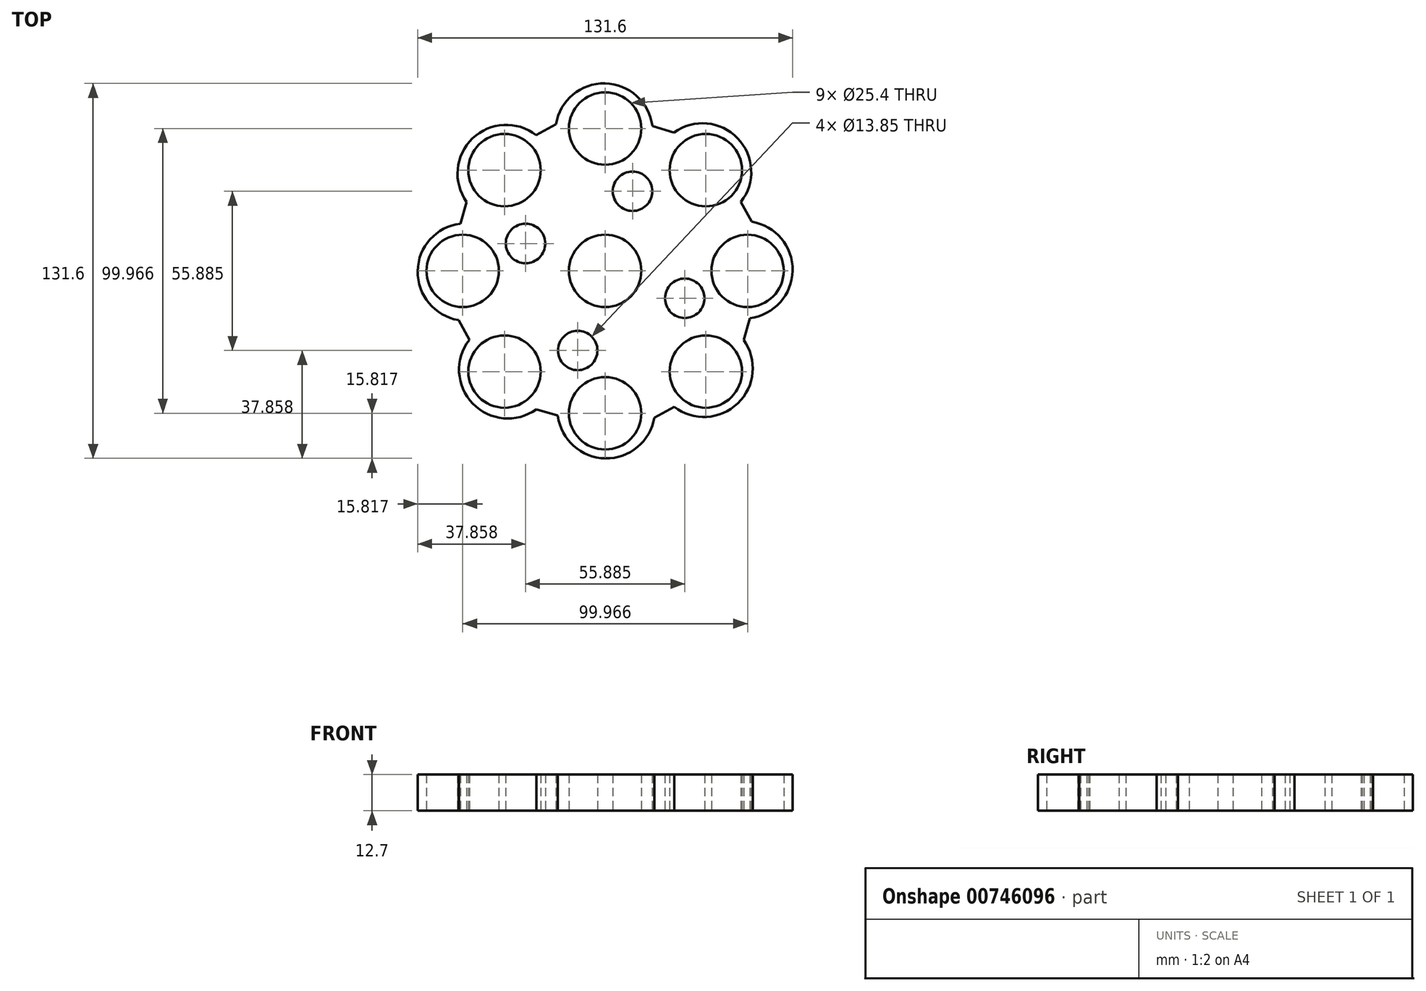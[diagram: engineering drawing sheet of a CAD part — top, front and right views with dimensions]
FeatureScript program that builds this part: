
annotation { "Feature Type Name" : "Feature", "Feature Type Description" : "" }
export const myFeature = defineFeature(function(context is Context, id is Id, definition is map)
    precondition{}
    {
        {
            var Q0;
            Q0=qCreatedBy(makeId("Top.planeOp"),FACE);
            var sketch = newSketch(context, id + "F0", { "sketchPlane" : qUnion([Q0])});
            skCircle(sketch, "E0", {"center": v(0, 0) * mm, "radius": 12.7 * mm});
            skCircle(sketch, "E1", {"center": v(0, 49.98) * mm, "radius": 12.7 * mm});
            skCircle(sketch, "E2.1.0", {"center": v(-35.34, 35.34) * mm, "radius": 12.7 * mm});
            skCircle(sketch, "E2.2.0", {"center": v(-49.98, 0) * mm, "radius": 12.7 * mm});
            skCircle(sketch, "E2.3.0", {"center": v(-35.34, -35.34) * mm, "radius": 12.7 * mm});
            skCircle(sketch, "E2.4.0", {"center": v(0, -49.98) * mm, "radius": 12.7 * mm});
            skCircle(sketch, "E2.5.0", {"center": v(35.34, -35.34) * mm, "radius": 12.7 * mm});
            skCircle(sketch, "E2.6.0", {"center": v(49.98, 0) * mm, "radius": 12.7 * mm});
            skCircle(sketch, "E2.7.0", {"center": v(35.34, 35.34) * mm, "radius": 12.7 * mm});
            skArc(sketch, "E3", {"start": v(16.58, 50.83) * mm, "mid": v(-0.06, 65.8) * mm, "end": v(-17.26, 51.47) * mm});
            skArc(sketch, "E4.1.0", {"start": v(-24.21, 47.66) * mm, "mid": v(-46.57, 46.49) * mm, "end": v(-48.6, 24.2) * mm});
            skArc(sketch, "E4.2.0", {"start": v(-50.83, 16.58) * mm, "mid": v(-65.8, -0.06) * mm, "end": v(-51.47, -17.26) * mm});
            skArc(sketch, "E4.3.0", {"start": v(-47.66, -24.21) * mm, "mid": v(-46.49, -46.57) * mm, "end": v(-24.2, -48.6) * mm});
            skArc(sketch, "E4.4.0", {"start": v(-16.58, -50.83) * mm, "mid": v(0.06, -65.8) * mm, "end": v(17.26, -51.47) * mm});
            skArc(sketch, "E4.5.0", {"start": v(24.21, -47.66) * mm, "mid": v(46.57, -46.49) * mm, "end": v(48.6, -24.2) * mm});
            skArc(sketch, "E4.6.0", {"start": v(50.83, -16.58) * mm, "mid": v(65.8, 0.06) * mm, "end": v(51.47, 17.26) * mm});
            skArc(sketch, "E4.7.0", {"start": v(47.66, 24.21) * mm, "mid": v(46.49, 46.57) * mm, "end": v(24.2, 48.6) * mm});
            skLineSegment(sketch, "E5", {"start": v(-24.21, 47.66) * mm, "end": v(-17.26, 51.47) * mm});
            skLineSegment(sketch, "E6.1.0", {"start": v(-50.83, 16.58) * mm, "end": v(-48.6, 24.2) * mm});
            skLineSegment(sketch, "E6.2.0", {"start": v(-47.66, -24.21) * mm, "end": v(-51.47, -17.26) * mm});
            skLineSegment(sketch, "E6.3.0", {"start": v(-16.58, -50.83) * mm, "end": v(-24.2, -48.6) * mm});
            skLineSegment(sketch, "E6.4.0", {"start": v(24.21, -47.66) * mm, "end": v(17.26, -51.47) * mm});
            skLineSegment(sketch, "E6.5.0", {"start": v(50.83, -16.58) * mm, "end": v(48.6, -24.2) * mm});
            skLineSegment(sketch, "E6.6.0", {"start": v(47.66, 24.21) * mm, "end": v(51.47, 17.26) * mm});
            skLineSegment(sketch, "E6.7.0", {"start": v(16.58, 50.83) * mm, "end": v(24.2, 48.6) * mm});
            skCircle(sketch, "E7", {"center": v(-27.94, 9.62) * mm, "radius": 6.93 * mm});
            skCircle(sketch, "E8.1.0", {"center": v(-9.62, -27.94) * mm, "radius": 6.93 * mm});
            skCircle(sketch, "E8.2.0", {"center": v(27.94, -9.62) * mm, "radius": 6.93 * mm});
            skCircle(sketch, "E8.3.0", {"center": v(9.62, 27.94) * mm, "radius": 6.93 * mm});
            skSolve(sketch);
        }
        {
            var Q0;
            Q0=makeQuery(id+"F0.imprint","IMPRINT",FACE,{"disambiguationData":[TD([[makeQuery(id+"F0.imprint","IMPRINT",EDGE,{"derivedFrom":sQuery(id+"F0.wireOp",EDGE,"E0")}),-1.0]])]});
            extrude(context, id + "F1", {"entities" : qUnion([Q0]), "depth" : 12.7 * mm, "offsetDistance" : 25.4 * mm});
        }
    });
